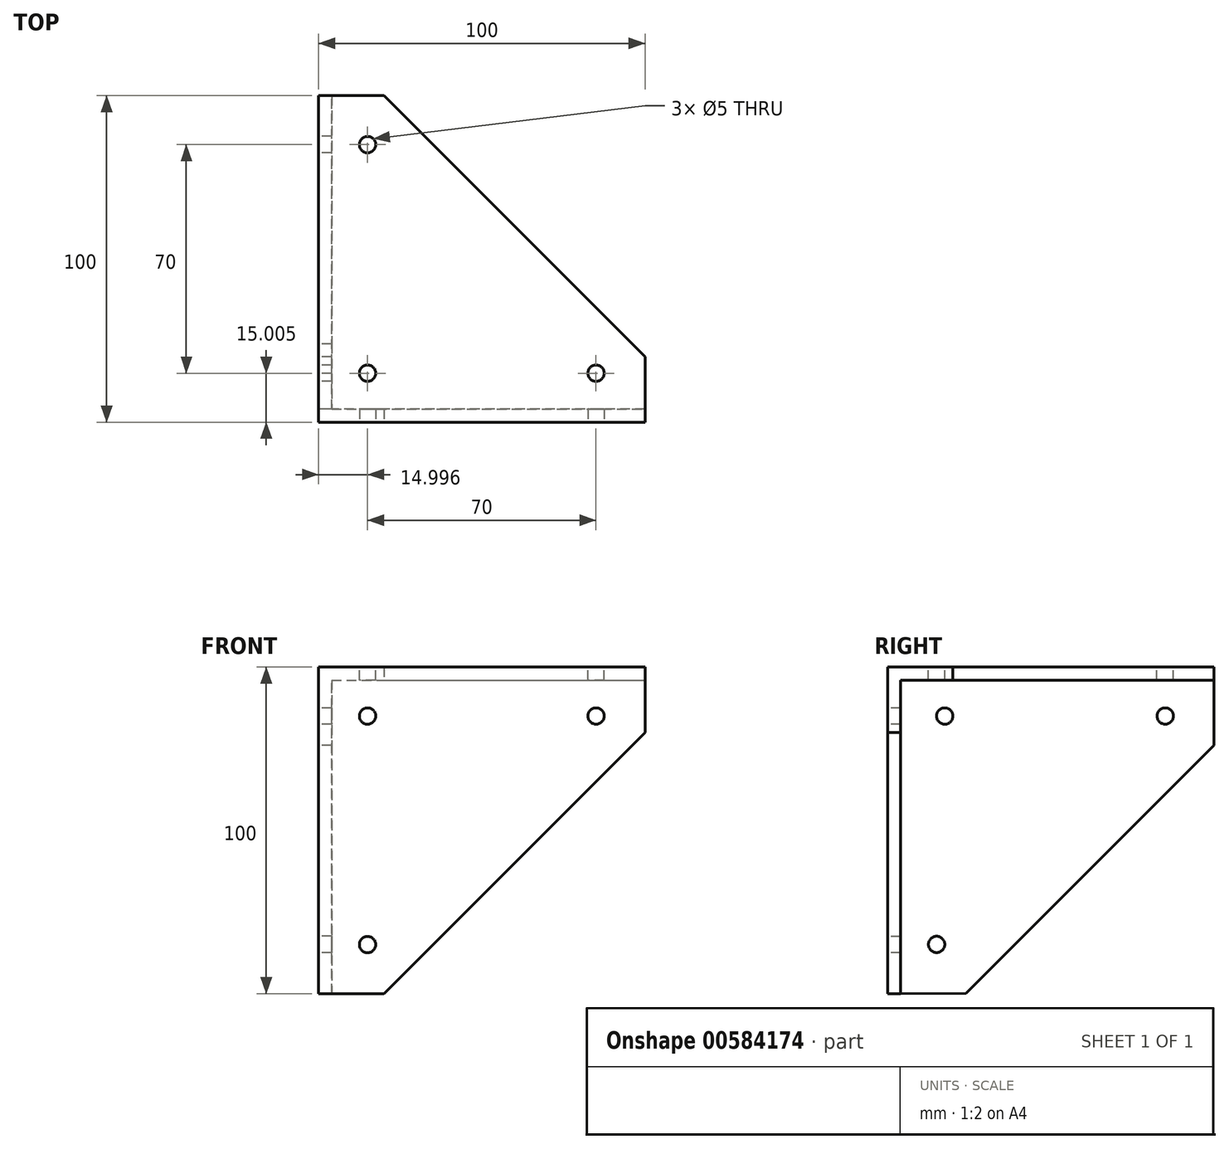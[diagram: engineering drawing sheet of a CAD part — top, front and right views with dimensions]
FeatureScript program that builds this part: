
annotation { "Feature Type Name" : "Feature", "Feature Type Description" : "" }
export const myFeature = defineFeature(function(context is Context, id is Id, definition is map)
    precondition{}
    {
        {
            var Q0;
            Q0=qCreatedBy(makeId("Top.planeOp"),FACE);
            var sketch = newSketch(context, id + "F0", { "sketchPlane" : qUnion([Q0])});
            skLineSegment(sketch, "E0", {"start": v(-48.66, 61.63) * mm, "end": v(-28.66, 61.63) * mm});
            skLineSegment(sketch, "E1", {"start": v(-28.66, 61.63) * mm, "end": v(51.34, -18.37) * mm});
            skLineSegment(sketch, "E2", {"start": v(51.34, -18.37) * mm, "end": v(51.34, -38.37) * mm});
            skLineSegment(sketch, "E3", {"start": v(51.34, -38.37) * mm, "end": v(-48.66, -38.37) * mm});
            skLineSegment(sketch, "E4", {"start": v(-48.66, -38.37) * mm, "end": v(-48.66, 61.63) * mm});
            skSolve(sketch);
        }
        {
            var Q0;
            Q0 = qSketchRegion(id + "F0", true);
            extrude(context, id + "F1", {"entities" : qUnion([Q0]), "depth" : 4 * mm, "offsetDistance" : 25 * mm});
        }
        {
            var Q0;
            Q0=makeQuery(id+"F1.opExtrude","SWEPT_FACE",FACE,{"disambiguationData":[OSD([sQuery(id+"F0.wireOp",EDGE,"E4")])]});
            cPlane(context, id + "F2", {"entities" : qUnion([Q0]), "cplaneType" : CPlaneType.OFFSET, "offset" : 0 * mm, "width" : 150 * mm, "height" : 150 * mm});
        }
        {
            var Q0;
            Q0=qCreatedBy(id+"F2.planeOp",FACE);
            var sketch = newSketch(context, id + "F3", { "sketchPlane" : qUnion([Q0])});
            skLineSegment(sketch, "E5", {"start": v(-61.63, 0) * mm, "end": v(-61.63, -20) * mm});
            skLineSegment(sketch, "E6", {"start": v(-61.63, -20) * mm, "end": v(14.37, -95.91) * mm});
            skLineSegment(sketch, "E7", {"start": v(38.37, -96) * mm, "end": v(38.37, 0) * mm});
            skLineSegment(sketch, "E8", {"start": v(38.37, 0) * mm, "end": v(-61.63, 0) * mm});
            skLineSegment(sketch, "E9", {"start": v(14.37, -95.91) * mm, "end": v(38.37, -96) * mm});
            skSolve(sketch);
        }
        {
            var Q0;
            Q0 = qSketchRegion(id + "F3", true);
            extrude(context, id + "F4", {"entities" : qUnion([Q0]), "oppositeDirection" : true, "depth" : 4 * mm, "offsetDistance" : 25 * mm});
        }
        {
            var Q0;
            Q0=makeQuery(id+"F4.opExtrude","SWEPT_FACE",FACE,{"disambiguationData":[OSD([sQuery(id+"F3.wireOp",EDGE,"E7")])]});
            var Q1;
            Q1=makeQuery(id+"F1.opExtrude","SWEPT_FACE",FACE,{"disambiguationData":[OSD([sQuery(id+"F0.wireOp",EDGE,"E3")])]});
            cPlane(context, id + "F5", {"entities" : qUnion([Q0, Q1]), "cplaneType" : CPlaneType.MID_PLANE, "offset" : 25 * mm, "width" : 150 * mm, "height" : 150 * mm});
        }
        {
            var Q0;
            Q0=qCreatedBy(id+"F5.planeOp",FACE);
            var sketch = newSketch(context, id + "F6", { "sketchPlane" : qUnion([Q0])});
            skLineSegment(sketch, "E10", {"start": v(-48.66, -96) * mm, "end": v(-28.66, -96) * mm});
            skLineSegment(sketch, "E11", {"start": v(-48.66, -96) * mm, "end": v(-48.66, 4) * mm});
            skSolve(sketch);
        }
        {
            var Q0;
            Q0=makeQuery(id+"F1.opExtrude","SWEPT_FACE",FACE,{"disambiguationData":[OSD([sQuery(id+"F0.wireOp",EDGE,"E3")])]});
            cPlane(context, id + "F7", {"entities" : qUnion([Q0]), "cplaneType" : CPlaneType.OFFSET, "offset" : 0 * mm, "width" : 150 * mm, "height" : 150 * mm});
        }
        {
            var Q0;
            Q0=qCreatedBy(id+"F7.planeOp",FACE);
            var sketch = newSketch(context, id + "F8", { "sketchPlane" : qUnion([Q0])});
            skLineSegment(sketch, "E12", {"start": v(51.34, 4) * mm, "end": v(51.34, -16) * mm});
            skLineSegment(sketch, "E13", {"start": v(51.34, -16) * mm, "end": v(-28.66, -96) * mm});
            skLineSegment(sketch, "E14", {"start": v(-28.66, -96) * mm, "end": v(-48.66, -96) * mm});
            skLineSegment(sketch, "E15", {"start": v(51.34, 4) * mm, "end": v(-48.66, 4) * mm});
            skLineSegment(sketch, "E16", {"start": v(-48.66, 4) * mm, "end": v(-48.66, -96) * mm});
            skSolve(sketch);
        }
        {
            var Q0;
            Q0 = qSketchRegion(id + "F8", true);
            extrude(context, id + "F9", {"entities" : qUnion([Q0]), "operationType" : NewBodyOperationType.ADD, "oppositeDirection" : true, "depth" : 4 * mm, "offsetDistance" : 25 * mm});
        }
        {
            var Q0;
            Q0=makeQuery(id+"F9.boolean.opBoolean","MERGE",FACE,{"derivedFrom":[makeQuery(id+"F1.opExtrude","SWEPT_FACE",FACE,{"disambiguationData":[OSD([sQuery(id+"F0.wireOp",EDGE,"E3")])]}),makeQuery(id+"F9.opExtrude","CAP_FACE",FACE,{"disambiguationData":[OSD([sQuery(id+"F8.wireOp",EDGE,"E12"),sQuery(id+"F8.wireOp",EDGE,"E13"),sQuery(id+"F8.wireOp",EDGE,"E14"),sQuery(id+"F8.wireOp",EDGE,"E15"),sQuery(id+"F8.wireOp",EDGE,"E16")])],"isStart":true})]});
            var sketch = newSketch(context, id + "F10", { "sketchPlane" : qUnion([Q0])});
            skCircle(sketch, "E17", {"center": v(36.34, -11) * mm, "radius": 2 * mm});
            skCircle(sketch, "E18", {"center": v(-33.66, -11) * mm, "radius": 2 * mm});
            skCircle(sketch, "E19", {"center": v(-33.66, -81) * mm, "radius": 2 * mm});
            skSolve(sketch);
        }
        {
            var Q0;
            Q0 = qSketchRegion(id + "F10", true);
            extrude(context, id + "F11", {"entities" : qUnion([Q0]), "operationType" : NewBodyOperationType.REMOVE, "oppositeDirection" : true, "depth" : 4 * mm, "offsetDistance" : 25 * mm});
        }
        {
            var Q0;
            Q0=makeQuery(id+"F9.boolean.opBoolean","MERGE",FACE,{"derivedFrom":[makeQuery(id+"F1.opExtrude","SWEPT_FACE",FACE,{"disambiguationData":[OSD([sQuery(id+"F0.wireOp",EDGE,"E3")])]}),makeQuery(id+"F9.opExtrude","CAP_FACE",FACE,{"disambiguationData":[OSD([sQuery(id+"F8.wireOp",EDGE,"E12"),sQuery(id+"F8.wireOp",EDGE,"E13"),sQuery(id+"F8.wireOp",EDGE,"E14"),sQuery(id+"F8.wireOp",EDGE,"E15"),sQuery(id+"F8.wireOp",EDGE,"E16")])],"isStart":true})]});
            var sketch = newSketch(context, id + "F12", { "sketchPlane" : qUnion([Q0])});
            skCircle(sketch, "E20", {"center": v(36.34, -11) * mm, "radius": 2.5 * mm});
            skCircle(sketch, "E21", {"center": v(-33.66, -11) * mm, "radius": 2.5 * mm});
            skCircle(sketch, "E22", {"center": v(-33.66, -81) * mm, "radius": 2.5 * mm});
            skSolve(sketch);
        }
        {
            var Q0;
            Q0 = qSketchRegion(id + "F12", true);
            extrude(context, id + "F13", {"entities" : qUnion([Q0]), "operationType" : NewBodyOperationType.REMOVE, "oppositeDirection" : true, "depth" : 4 * mm, "offsetDistance" : 25 * mm});
        }
        {
            var Q0;
            Q0=makeQuery(id+"F4.opExtrude","CAP_FACE",FACE,{"disambiguationData":[OSD([sQuery(id+"F3.wireOp",EDGE,"E5"),sQuery(id+"F3.wireOp",EDGE,"E6"),sQuery(id+"F3.wireOp",EDGE,"E7"),sQuery(id+"F3.wireOp",EDGE,"E8"),sQuery(id+"F3.wireOp",EDGE,"E9")])],"isStart":true});
            var sketch = newSketch(context, id + "F14", { "sketchPlane" : qUnion([Q0])});
            skCircle(sketch, "E23", {"center": v(-46.67, -11) * mm, "radius": 2.5 * mm});
            skCircle(sketch, "E24", {"center": v(20.87, -11) * mm, "radius": 2.5 * mm});
            skCircle(sketch, "E25", {"center": v(23.37, -80.95) * mm, "radius": 2.5 * mm});
            skSolve(sketch);
        }
        {
            var Q0;
            Q0 = qSketchRegion(id + "F14", true);
            extrude(context, id + "F15", {"entities" : qUnion([Q0]), "operationType" : NewBodyOperationType.REMOVE, "oppositeDirection" : true, "depth" : 4 * mm, "offsetDistance" : 25 * mm});
        }
        {
            var Q0;
            Q0=makeQuery(id+"F1.opExtrude","CAP_FACE",FACE,{"disambiguationData":[OSD([sQuery(id+"F0.wireOp",EDGE,"E0"),sQuery(id+"F0.wireOp",EDGE,"E1"),sQuery(id+"F0.wireOp",EDGE,"E2"),sQuery(id+"F0.wireOp",EDGE,"E3"),sQuery(id+"F0.wireOp",EDGE,"E4")])],"isStart":false});
            var sketch = newSketch(context, id + "F16", { "sketchPlane" : qUnion([Q0])});
            skCircle(sketch, "E26", {"center": v(-33.66, 46.63) * mm, "radius": 2.5 * mm});
            skCircle(sketch, "E27", {"center": v(-33.66, -23.37) * mm, "radius": 2.5 * mm});
            skCircle(sketch, "E28", {"center": v(36.34, -23.37) * mm, "radius": 2.5 * mm});
            skSolve(sketch);
        }
        {
            var Q0;
            Q0 = qSketchRegion(id + "F16", true);
            extrude(context, id + "F17", {"entities" : qUnion([Q0]), "operationType" : NewBodyOperationType.REMOVE, "oppositeDirection" : true, "depth" : 4 * mm, "offsetDistance" : 25 * mm});
        }
    });
